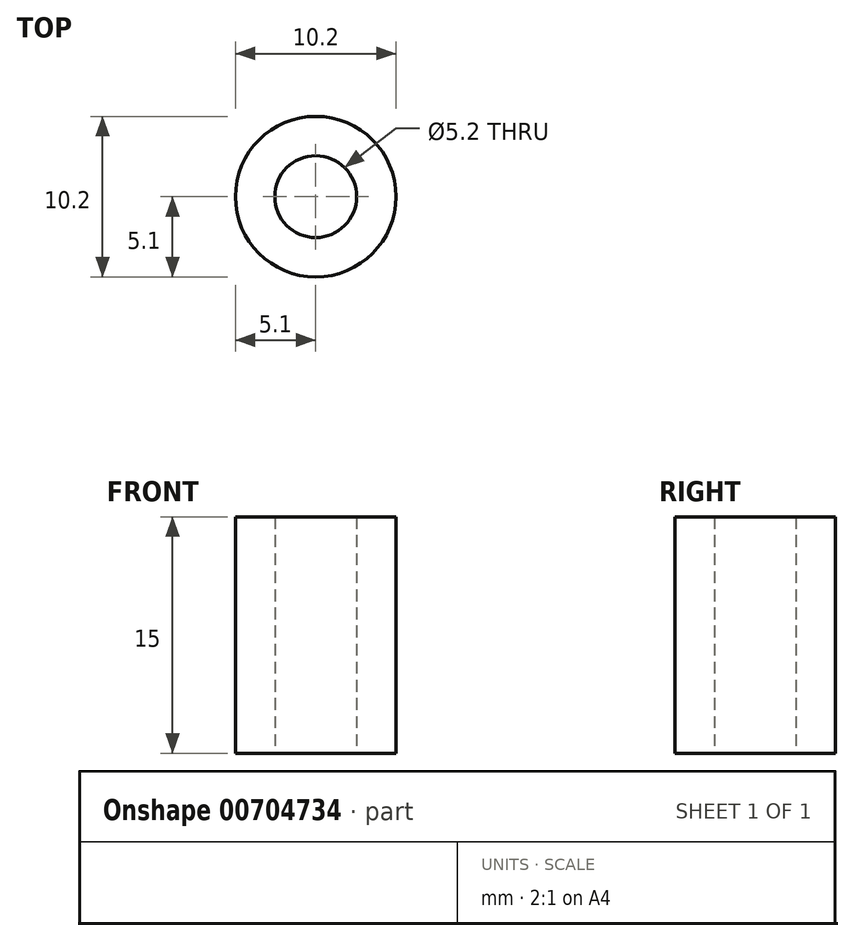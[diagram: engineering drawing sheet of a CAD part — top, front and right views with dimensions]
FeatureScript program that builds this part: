
annotation { "Feature Type Name" : "Feature", "Feature Type Description" : "" }
export const myFeature = defineFeature(function(context is Context, id is Id, definition is map)
    precondition{}
    {
        {
            var Q0;
            Q0=qCreatedBy(makeId("Top.planeOp"),FACE);
            var sketch = newSketch(context, id + "F0", { "sketchPlane" : qUnion([Q0])});
            skCircle(sketch, "E0", {"center": v(0, 0) * mm, "radius": 5.1 * mm});
            skCircle(sketch, "E1", {"center": v(0, 0) * mm, "radius": 2.6 * mm});
            skSolve(sketch);
        }
        {
            var Q0;
            Q0=makeQuery(id+"F0.imprint","IMPRINT",FACE,{"disambiguationData":[TD([[makeQuery(id+"F0.imprint","IMPRINT",EDGE,{"derivedFrom":sQuery(id+"F0.wireOp",EDGE,"E0")}),1.0]])]});
            extrude(context, id + "F1", {"entities" : qUnion([Q0]), "depth" : 15 * mm, "offsetDistance" : 25 * mm});
        }
    });
